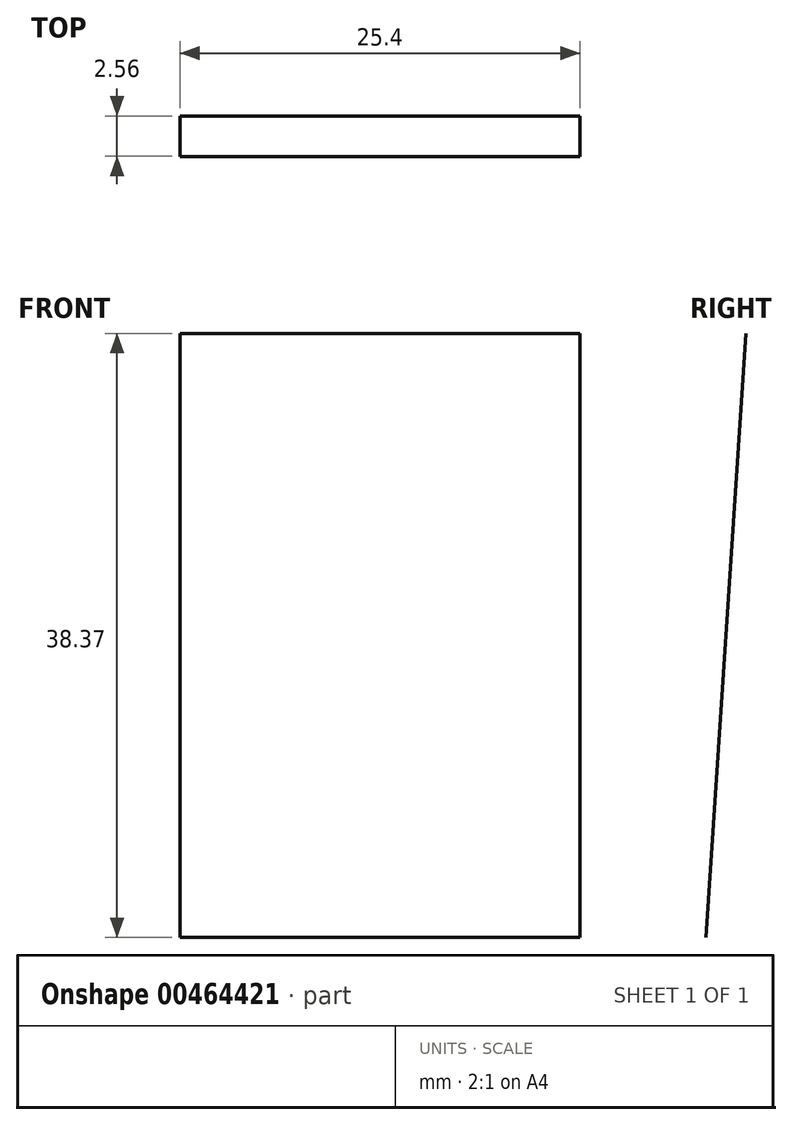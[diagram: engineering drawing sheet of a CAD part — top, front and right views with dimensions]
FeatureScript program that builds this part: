
annotation { "Feature Type Name" : "Feature", "Feature Type Description" : "" }
export const myFeature = defineFeature(function(context is Context, id is Id, definition is map)
    precondition{}
    {
        {
            var Q0;
            Q0=qCreatedBy(makeId("Right.planeOp"),FACE);
            var sketch = newSketch(context, id + "F0", { "sketchPlane" : qUnion([Q0])});
            skLineSegment(sketch, "E0", {"start": v(62.57, 44.89) * mm, "end": v(30.93, 44.66) * mm});
            skLineSegment(sketch, "E1", {"start": v(30.93, 44.66) * mm, "end": v(30, 23.5) * mm});
            skLineSegment(sketch, "E2", {"start": v(30, 23.5) * mm, "end": v(4.42, 23.03) * mm});
            skLineSegment(sketch, "E3", {"start": v(4.42, 23.03) * mm, "end": v(4.42, 6.05) * mm});
            skLineSegment(sketch, "E4", {"start": v(4.42, 6.05) * mm, "end": v(60, 6.75) * mm});
            skLineSegment(sketch, "E5", {"start": v(60, 6.75) * mm, "end": v(62.57, 45.12) * mm});
            skSolve(sketch);
        }
        {
            var Q0;
            Q0=sQuery(id+"F0.wireOp",EDGE,"E5");
            extrude(context, id + "F1", {"bodyType" : ToolBodyType.SURFACE, "surfaceEntities" : qUnion([Q0]), "depth" : 25.4 * mm});
        }
    });
